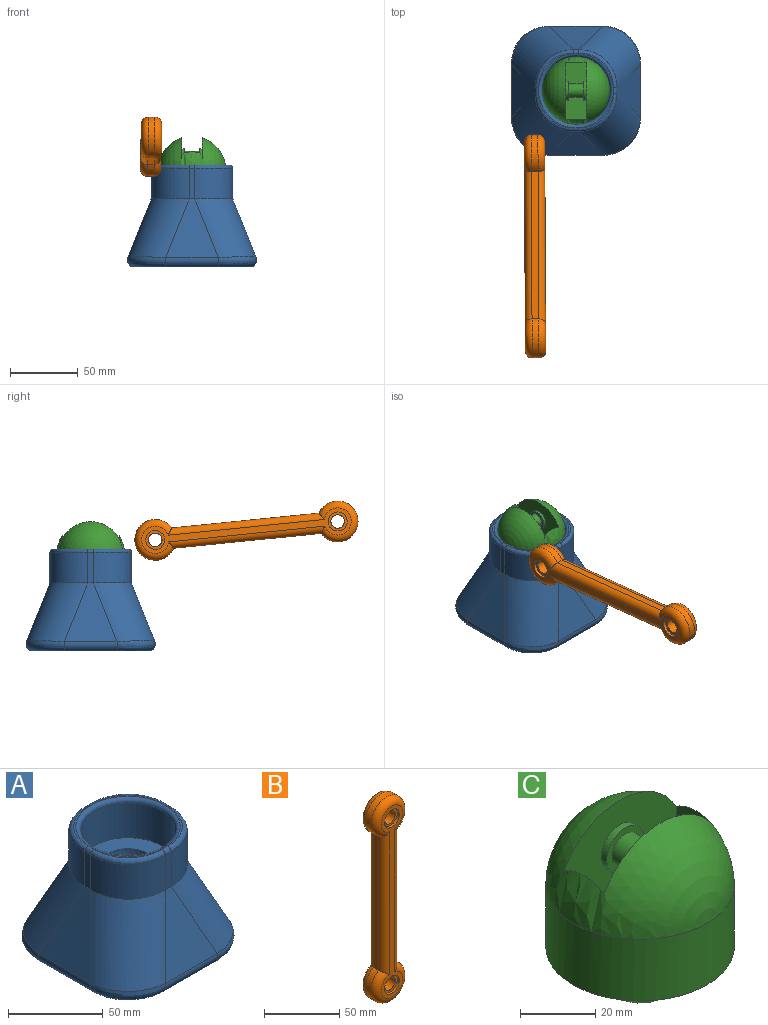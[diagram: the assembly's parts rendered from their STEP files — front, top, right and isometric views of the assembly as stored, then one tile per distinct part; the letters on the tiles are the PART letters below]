
ASSEMBLY  parts=3 mates=1
PART A: 41 faces, bbox 100.2x100.2x75 mm
  f0: plane 27.5x27.5mm, normal (0,0,1), area 30.8mm2, adj f32,f33,f34,f35
  f1: plane 27.5x27.5mm, normal (0,0,1), area 30.8mm2, adj f32,f34,f36,f38
  f2: plane 27.5x27.5mm, normal (0,0,1), area 30.8mm2, adj f32,f38,f39,f40
  f3: plane 85.23x85.23mm, normal (0,0,-1), area 6821.3mm2, adj f8,f9,f10,f11,f13,f15,f17,f19
  f4: plane 43.14x38.81mm, normal (0,-0.93,0.37), area 1001.3mm2, adj f10,f14,f18,f21
  f5: plane 43.14x38.81mm, normal (0.93,0,0.37), area 1001.3mm2, adj f8,f16,f18,f23
  f6: plane 43.14x38.81mm, normal (0,0.93,0.37), area 1001.3mm2, adj f9,f12,f16,f25
  f7: plane 43.14x38.81mm, normal (-0.93,0,0.37), area 1001.3mm2, adj f11,f12,f14,f28
  f8: cylinder r=5mm len=38.81mm, axis (0,-1,0), area 378.6mm2, adj f3,f5,f17,f19
  f9: cylinder r=5mm len=38.81mm, axis (-1,0,0), area 378.6mm2, adj f3,f6,f13,f17
  f10: cylinder r=5mm len=38.81mm, axis (-1,0,0), area 378.6mm2, adj f3,f4,f15,f19
  f11: cylinder r=5mm len=38.81mm, axis (0,-1,0), area 378.6mm2, adj f3,f7,f13,f15
  f12: cylinder r=30mm len=49.81mm, axis (0.35,-0.35,0.87), area 2110.3mm2, adj f6,f7,f13,f26
  f13: bspline ~34.54x34.54mm, area 430.9mm2, adj f3,f9,f11,f12
  f14: cylinder r=30mm len=49.81mm, axis (-0.35,-0.35,-0.87), area 2110.3mm2, adj f4,f7,f15,f20
  f15: bspline ~28.22x28.22mm, area 430.9mm2, adj f3,f10,f11,f14
  f16: cylinder r=30mm len=49.81mm, axis (0.35,0.35,-0.87), area 2110.3mm2, adj f5,f6,f17,f24
  f17: bspline ~28.22x28.22mm, area 430.9mm2, adj f3,f8,f9,f16
  f18: cylinder r=30mm len=49.81mm, axis (-0.35,0.35,0.87), area 2110.3mm2, adj f4,f5,f19,f22
  f19: bspline ~34.54x34.54mm, area 430.9mm2, adj f3,f8,f10,f18
  f20: extruded ~27.85x27.85mm, area 990.3mm2, adj f14,f21,f28,f37
  f21: plane 22.5x4.29mm, normal (0,-1,0), area 96.6mm2, adj f4,f20,f22,f35
  f22: extruded ~27.85x27.85mm, area 990.3mm2, adj f18,f21,f23,f33
  f23: plane 22.5x4.29mm, normal (1,0,0), area 96.6mm2, adj f5,f22,f24,f34
  f24: extruded ~27.85x27.85mm, area 990.3mm2, adj f16,f23,f25,f36
  f25: plane 22.5x4.29mm, normal (0,1,0), area 96.6mm2, adj f6,f24,f26,f38
  f26: extruded ~27.85x27.85mm, area 990.3mm2, adj f12,f25,f28,f40
  f27: cylinder r=25mm len=50mm, axis (0,0,-1), area 3534.3mm2, adj f31,f32
  f28: plane 22.5x4.29mm, normal (-1,0,0), area 96.6mm2, adj f7,f20,f26,f39
  f29: plane 27.5x27.5mm, normal (0,0,1), area 30.8mm2, adj f32,f35,f37,f39
  f30: sphere r=15mm, area 1413.7mm2, adj f31
  f31: plane 50x50mm, normal (0,0,1), area 1256.6mm2, adj f27,f30
  f32: torus R=27.5mm, axis (0,0,1), area 639.3mm2, adj f0,f1,f2,f27,f29
  f33: bspline ~32.23x32.23mm, area 167.2mm2, adj f0,f22,f34,f35
  f34: cylinder r=2.5mm len=4.29mm, axis (0,-1,0), area 16.9mm2, adj f0,f1,f23,f33,f36
  f35: cylinder r=2.5mm len=4.29mm, axis (-1,0,0), area 16.9mm2, adj f0,f21,f29,f33,f37
  f36: bspline ~32.23x32.23mm, area 167.2mm2, adj f1,f24,f34,f38
  f37: bspline ~32.23x32.23mm, area 167.2mm2, adj f20,f29,f35,f39
  f38: cylinder r=2.5mm len=4.29mm, axis (1,0,0), area 16.9mm2, adj f1,f2,f25,f36,f40
  f39: cylinder r=2.5mm len=4.29mm, axis (0,1,0), area 16.9mm2, adj f2,f28,f29,f37,f40
  f40: bspline ~32.23x32.23mm, area 167.2mm2, adj f2,f26,f38,f39
PART B: 24 faces, bbox 32.5x15x167.5 mm
  f0: cylinder r=5mm len=11mm, axis (0,-1,0), area 345.6mm2, adj f19,f22
  f1: cylinder r=5mm len=11mm, axis (0,-1,0), area 345.6mm2, adj f17,f20
  f2: plane 109.02x5mm, normal (1,0,0), area 545.1mm2, adj f3,f5,f8,f12
  f3: cylinder r=15mm len=30mm, axis (0,1,0), area 392.7mm2, adj f2,f4,f9,f13
  f4: plane 109.02x5mm, normal (-1,0,0), area 545.1mm2, adj f3,f5,f11,f15
  f5: cylinder r=15mm len=30mm, axis (0,1,0), area 392.7mm2, adj f2,f4,f10,f14
  f6: plane 155x20mm, normal (0,-1,0), area 896.5mm2, adj f12,f13,f14,f15,f16,f18
  f7: plane 155x20mm, normal (0,1,0), area 896.5mm2, adj f8,f9,f10,f11,f21,f23
  f8: cylinder r=5mm len=115.64mm, axis (0,0,1), area 874.1mm2, adj f2,f7,f9,f10
  f9: torus R=10mm, axis (0,-1,0), area 558mm2, adj f3,f7,f8,f11
  f10: torus R=10mm, axis (0,-1,0), area 558mm2, adj f5,f7,f8,f11
  f11: cylinder r=5mm len=115.64mm, axis (0,0,-1), area 874.1mm2, adj f4,f7,f9,f10
  f12: cylinder r=5mm len=115.64mm, axis (0,0,-1), area 874.1mm2, adj f2,f6,f13,f14
  f13: torus R=10mm, axis (0,-1,0), area 558mm2, adj f3,f6,f12,f15
  f14: torus R=10mm, axis (0,-1,0), area 558mm2, adj f5,f6,f12,f15
  f15: cylinder r=5mm len=115.64mm, axis (0,0,1), area 874.1mm2, adj f4,f6,f13,f14
  f16: cylinder r=7mm len=14mm, axis (0,-1,0), area 88mm2, adj f6,f17
  f17: plane 14x14mm, normal (0,-1,0), area 75.4mm2, adj f1,f16
  f18: cylinder r=7mm len=14mm, axis (0,-1,0), area 88mm2, adj f6,f19
  f19: plane 14x14mm, normal (0,-1,0), area 75.4mm2, adj f0,f18
  f20: plane 14x14mm, normal (0,1,0), area 75.4mm2, adj f1,f21
  f21: cylinder r=7mm len=14mm, axis (0,1,0), area 88mm2, adj f7,f20
  f22: plane 14x14mm, normal (0,1,0), area 75.4mm2, adj f0,f23
  f23: cylinder r=7mm len=14mm, axis (0,1,0), area 88mm2, adj f7,f22
PART C: 14 faces, bbox 50x50x60 mm
  f0: sphere r=25mm, area 3160.2mm2, adj f1,f4,f5,f6,f7
  f1: cylinder r=25mm len=50mm, axis (0,0,1), area 3141.6mm2, adj f0,f2
  f2: plane 50x50mm, normal (0,0,-1), area 1256.6mm2, adj f1,f3
  f3: sphere r=15mm, area 1413.7mm2, adj f2
  f4: plane 28.56x15mm, normal (-1,0,0), area 417.6mm2, adj f0,f5,f7,f8
  f5: plane 42x38.85mm, normal (0,1,0), area 1326mm2, adj f0,f4,f6,f8,f9
  f6: plane 28.56x15mm, normal (1,0,0), area 417.6mm2, adj f0,f5,f7,f8
  f7: plane 42x38.85mm, normal (0,-1,0), area 1326mm2, adj f0,f4,f6,f8,f12
  f8: plane 42x15mm, normal (0,0,1), area 630mm2, adj f4,f5,f6,f7
  f9: cylinder r=7mm len=14mm, axis (0,-1,0), area 88mm2, adj f5,f10
  f10: plane 14x14mm, normal (0,1,0), area 75.4mm2, adj f9,f11
  f11: cylinder r=5mm len=11mm, axis (0,-1,0), area 345.6mm2, adj f10,f13
  f12: cylinder r=7mm len=14mm, axis (0,1,0), area 88mm2, adj f7,f13
  f13: plane 14x14mm, normal (0,-1,0), area 75.4mm2, adj f11,f12
PLACE A t=(-68.74,-12.86,34.44)mm fixed
PLACE B rot(axis=(-0.6,0.59,0.54),123.5deg) t=(-56.13,-130.85,270.78)mm
PLACE C rot(axis=(0,0,-1),89.7deg) t=(-67.44,-72.26,105.69)mm
MATE revolute A.f27 <-> C.f1  axis (0,0,-1) through (-18.74,37.14,95.69)mm
